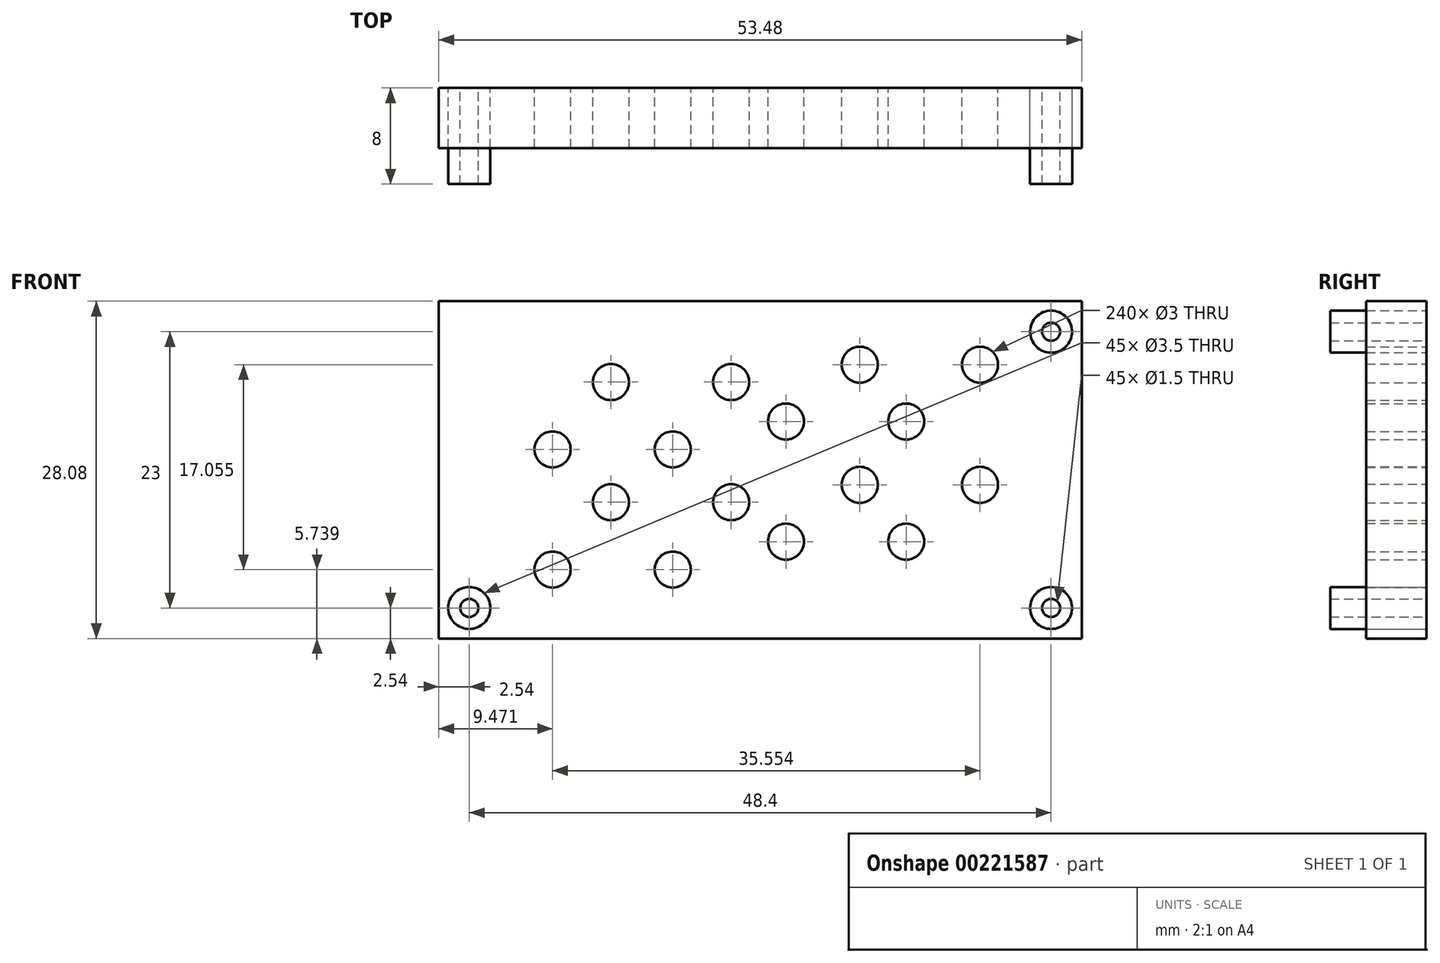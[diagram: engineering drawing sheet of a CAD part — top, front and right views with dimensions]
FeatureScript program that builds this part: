
annotation { "Feature Type Name" : "Feature", "Feature Type Description" : "" }
export const myFeature = defineFeature(function(context is Context, id is Id, definition is map)
    precondition{}
    {
        {
            var Q0;
            Q0=qCreatedBy(makeId("Front.planeOp"),FACE);
            var sketch = newSketch(context, id + "F0", { "sketchPlane" : qUnion([Q0])});
            skLineSegment(sketch, "E0.bottom", {"start": v(0, 0) * mm, "end": v(53.48, 0) * mm});
            skLineSegment(sketch, "E0.top", {"start": v(0, 28.08) * mm, "end": v(53.48, 28.08) * mm});
            skLineSegment(sketch, "E0.left", {"start": v(0, 0) * mm, "end": v(0, 28.08) * mm});
            skLineSegment(sketch, "E0.right", {"start": v(53.48, 0) * mm, "end": v(53.48, 28.08) * mm});
            skCircle(sketch, "E1", {"center": v(2.54, 2.54) * mm, "radius": 0.75 * mm});
            skCircle(sketch, "E2", {"center": v(50.94, 2.54) * mm, "radius": 0.75 * mm});
            skCircle(sketch, "E3", {"center": v(50.94, 25.54) * mm, "radius": 0.75 * mm});
            skCircle(sketch, "E4", {"center": v(2.54, 2.54) * mm, "radius": 1.75 * mm});
            skCircle(sketch, "E5", {"center": v(50.94, 25.54) * mm, "radius": 1.75 * mm});
            skCircle(sketch, "E6", {"center": v(50.94, 2.54) * mm, "radius": 1.75 * mm});
            skCircle(sketch, "E7", {"center": v(35.03, 22.8) * mm, "radius": 1.5 * mm});
            skCircle(sketch, "E8", {"center": v(45.03, 22.8) * mm, "radius": 1.5 * mm});
            skCircle(sketch, "E9", {"center": v(45.03, 12.8) * mm, "radius": 1.5 * mm});
            skCircle(sketch, "E10", {"center": v(35.03, 12.8) * mm, "radius": 1.5 * mm});
            skCircle(sketch, "E11", {"center": v(28.88, 18.06) * mm, "radius": 1.5 * mm});
            skCircle(sketch, "E12", {"center": v(38.88, 18.06) * mm, "radius": 1.5 * mm});
            skCircle(sketch, "E13", {"center": v(38.88, 8.06) * mm, "radius": 1.5 * mm});
            skCircle(sketch, "E14", {"center": v(28.88, 8.06) * mm, "radius": 1.5 * mm});
            skCircle(sketch, "E15", {"center": v(14.32, 21.34) * mm, "radius": 1.5 * mm});
            skCircle(sketch, "E16", {"center": v(24.32, 21.34) * mm, "radius": 1.5 * mm});
            skCircle(sketch, "E17", {"center": v(24.32, 11.34) * mm, "radius": 1.5 * mm});
            skCircle(sketch, "E18", {"center": v(14.32, 11.34) * mm, "radius": 1.5 * mm});
            skCircle(sketch, "E19", {"center": v(9.47, 15.74) * mm, "radius": 1.5 * mm});
            skCircle(sketch, "E20", {"center": v(19.47, 15.74) * mm, "radius": 1.5 * mm});
            skCircle(sketch, "E21", {"center": v(19.47, 5.74) * mm, "radius": 1.5 * mm});
            skCircle(sketch, "E22", {"center": v(9.47, 5.74) * mm, "radius": 1.5 * mm});
            skSolve(sketch);
        }
        {
            var Q0;
            Q0=makeQuery(id+"F0.imprint","IMPRINT",FACE,{"disambiguationData":[TD([[makeQuery(id+"F0.imprint","IMPRINT",EDGE,{"derivedFrom":sQuery(id+"F0.wireOp",EDGE,"E1")}),-1.0]])]});
            var Q1;
            Q1=makeQuery(id+"F0.imprint","IMPRINT",FACE,{"disambiguationData":[TD([[makeQuery(id+"F0.imprint","IMPRINT",EDGE,{"derivedFrom":sQuery(id+"F0.wireOp",EDGE,"E2")}),-1.0]])]});
            var Q2;
            Q2=makeQuery(id+"F0.imprint","IMPRINT",FACE,{"disambiguationData":[TD([[makeQuery(id+"F0.imprint","IMPRINT",EDGE,{"derivedFrom":sQuery(id+"F0.wireOp",EDGE,"E3")}),-1.0]])]});
            var Q3;
            Q3=sQuery(id+"F0.wireOp",EDGE,"E1");
            extrude(context, id + "F1", {"entities" : qUnion([Q0, Q1, Q2]), "surfaceEntities" : qUnion([Q3]), "depth" : 8 * mm});
        }
        {
            var Q0;
            Q0 = qSketchRegion(id + "F0", true);
            extrude(context, id + "F2", {"entities" : qUnion([Q0]), "depth" : 5 * mm});
        }
    });
